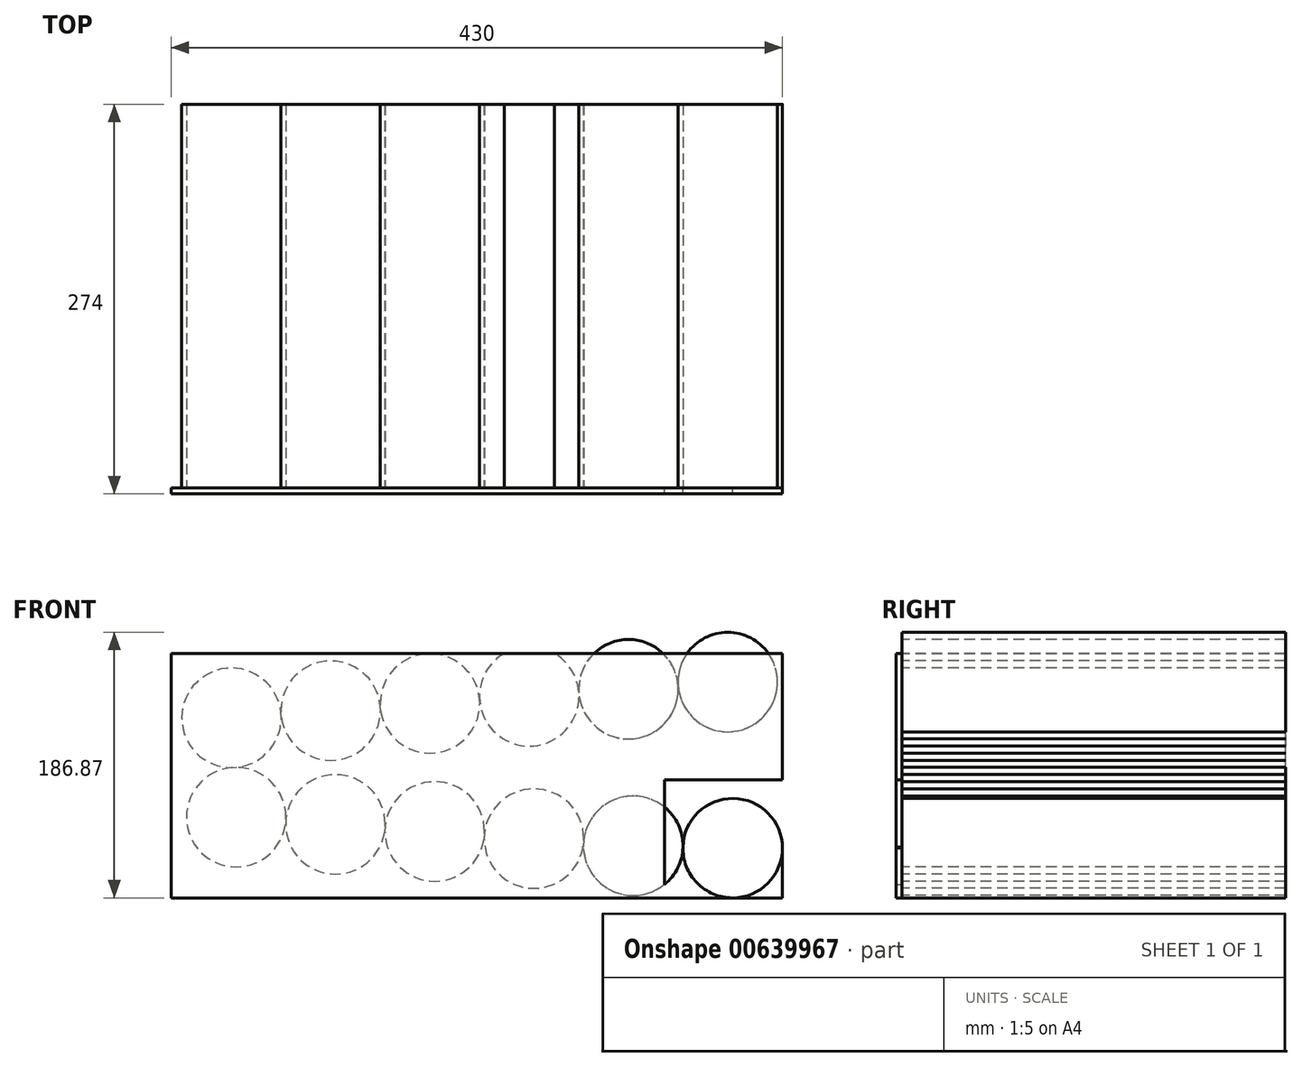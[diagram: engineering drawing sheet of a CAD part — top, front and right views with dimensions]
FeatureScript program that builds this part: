
annotation { "Feature Type Name" : "Feature", "Feature Type Description" : "" }
export const myFeature = defineFeature(function(context is Context, id is Id, definition is map)
    precondition{}
    {
        {
            var Q0;
            Q0=qCreatedBy(makeId("Front.planeOp"),FACE);
            var sketch = newSketch(context, id + "F0", { "sketchPlane" : qUnion([Q0])});
            skLineSegment(sketch, "E0.bottom", {"start": v(-430, 172) * mm, "end": v(0, 172) * mm});
            skLineSegment(sketch, "E0.top", {"start": v(-430, 0) * mm, "end": v(0, 0) * mm});
            skLineSegment(sketch, "E0.left", {"start": v(-430, 172) * mm, "end": v(-430, 0) * mm});
            skLineSegment(sketch, "E0.right", {"start": v(0, 172) * mm, "end": v(0, 0) * mm});
            skCircle(sketch, "E1", {"center": v(-35, 35) * mm, "radius": 35 * mm});
            skCircle(sketch, "E2", {"center": v(-244.62, 46.73) * mm, "radius": 35 * mm});
            skCircle(sketch, "E3", {"center": v(-104.98, 36.67) * mm, "radius": 35 * mm});
            skCircle(sketch, "E4", {"center": v(-174.8, 41.7) * mm, "radius": 35 * mm});
            skLineSegment(sketch, "E5", {"start": v(-430, 25) * mm, "end": v(-83, 0) * mm});
            skCircle(sketch, "E6", {"center": v(-314.44, 51.76) * mm, "radius": 35 * mm});
            skCircle(sketch, "E7", {"center": v(-384.26, 56.8) * mm, "radius": 35 * mm});
            skLineSegment(sketch, "E8", {"start": v(-347, 94.55) * mm, "end": v(0, 119.55) * mm});
            skLineSegment(sketch, "E9", {"start": v(0, 119.55) * mm, "end": v(-430, 119.55) * mm, "construction": true});
            skLineSegment(sketch, "E10", {"start": v(-453.18, 96.16) * mm, "end": v(39.92, 65.4) * mm, "construction": true});
            skLineSegment(sketch, "E11", {"start": v(-465.14, 101.92) * mm, "end": v(33.1, 70.83) * mm, "construction": true});
            skCircle(sketch, "E12", {"center": v(-387.54, 126.72) * mm, "radius": 35 * mm});
            skCircle(sketch, "E13", {"center": v(-317.72, 131.75) * mm, "radius": 35 * mm});
            skCircle(sketch, "E14", {"center": v(-247.9, 136.78) * mm, "radius": 35 * mm});
            skCircle(sketch, "E15", {"center": v(-178.08, 141.8) * mm, "radius": 35 * mm});
            skCircle(sketch, "E16", {"center": v(-108.26, 146.84) * mm, "radius": 35 * mm});
            skCircle(sketch, "E17", {"center": v(-38.44, 151.87) * mm, "radius": 35 * mm});
            skLineSegment(sketch, "E18.bottom", {"start": v(-83, 0) * mm, "end": v(0, 0) * mm});
            skLineSegment(sketch, "E18.top", {"start": v(-83, 83) * mm, "end": v(0, 83) * mm});
            skLineSegment(sketch, "E18.left", {"start": v(-83, 0) * mm, "end": v(-83, 83) * mm});
            skLineSegment(sketch, "E18.right", {"start": v(0, 0) * mm, "end": v(0, 83) * mm});
            skSolve(sketch);
        }
        {
            var Q0;
            {var subQ3=sQuery(id+"F0.wireOp",EDGE,"E0.left");var subQ4=sQuery(id+"F0.wireOp",EDGE,"E0.top");var subQ5=makeQuery(id+"F0.imprint","INTERSECT",VERTEX,{"derivedFrom":[subQ4,subQ3]});Q0=makeQuery(id+"F0.imprint","IMPRINT",FACE,{"disambiguationData":[TD([[makeQuery(id+"F0.imprint","IMPRINT",EDGE,{"disambiguationData":[TD([[subQ5,-1.0]])],"derivedFrom":subQ4}),1.0]])]});}
            var Q1;
            {var subQ0=sQuery(id+"F0.wireOp",EDGE,"E7");var subQ1=sQuery(id+"F0.wireOp",EDGE,"E5");var subQ2=makeQuery(id+"F0.imprint","INTERSECT",VERTEX,{"derivedFrom":[subQ1,subQ0]});Q1=makeQuery(id+"F0.imprint","IMPRINT",FACE,{"disambiguationData":[TD([[makeQuery(id+"F0.imprint","IMPRINT",EDGE,{"disambiguationData":[TD([[subQ2,-1.0]])],"derivedFrom":subQ1}),1.0]])]});}
            var Q2;
            {var subQ0=sQuery(id+"F0.wireOp",EDGE,"E7");var subQ1=makeQuery(id+"F0.imprint","INTERSECT",VERTEX,{"derivedFrom":[sQuery(id+"F0.wireOp",EDGE,"E5"),subQ0]});Q2=makeQuery(id+"F0.imprint","IMPRINT",FACE,{"disambiguationData":[TD([[makeQuery(id+"F0.imprint","IMPRINT",EDGE,{"disambiguationData":[TD([[subQ1,1.0]])],"derivedFrom":subQ0}),1.0]])]});}
            var Q3;
            {var subQ5=sQuery(id+"F0.wireOp",EDGE,"E0.left");var subQ12=sQuery(id+"F0.wireOp",EDGE,"E0.bottom");var subQ13=makeQuery(id+"F0.imprint","INTERSECT",VERTEX,{"derivedFrom":[subQ12,subQ5]});Q3=makeQuery(id+"F0.imprint","IMPRINT",FACE,{"disambiguationData":[TD([[makeQuery(id+"F0.imprint","IMPRINT",EDGE,{"disambiguationData":[TD([[subQ13,-1.0]])],"derivedFrom":subQ12}),-1.0]])]});}
            var Q4;
            {var subQ0=sQuery(id+"F0.wireOp",EDGE,"E6");var subQ1=makeQuery(id+"F0.imprint","INTERSECT",VERTEX,{"derivedFrom":[sQuery(id+"F0.wireOp",EDGE,"E5"),subQ0]});Q4=makeQuery(id+"F0.imprint","IMPRINT",FACE,{"disambiguationData":[TD([[makeQuery(id+"F0.imprint","IMPRINT",EDGE,{"disambiguationData":[TD([[subQ1,1.0]])],"derivedFrom":subQ0}),1.0]])]});}
            var Q5;
            {var subQ0=sQuery(id+"F0.wireOp",EDGE,"E5");var subQ1=sQuery(id+"F0.wireOp",EDGE,"E2");var subQ2=makeQuery(id+"F0.imprint","INTERSECT",VERTEX,{"derivedFrom":[subQ1,subQ0]});Q5=makeQuery(id+"F0.imprint","IMPRINT",FACE,{"disambiguationData":[TD([[makeQuery(id+"F0.imprint","IMPRINT",EDGE,{"disambiguationData":[TD([[subQ2,1.0]])],"derivedFrom":subQ1}),-1.0]])]});}
            var Q6;
            {var subQ0=sQuery(id+"F0.wireOp",EDGE,"E5");var subQ1=sQuery(id+"F0.wireOp",EDGE,"E2");var subQ2=makeQuery(id+"F0.imprint","INTERSECT",VERTEX,{"derivedFrom":[subQ1,subQ0]});Q6=makeQuery(id+"F0.imprint","IMPRINT",FACE,{"disambiguationData":[TD([[makeQuery(id+"F0.imprint","IMPRINT",EDGE,{"disambiguationData":[TD([[subQ2,-1.0]])],"derivedFrom":subQ1}),-1.0]])]});}
            var Q7;
            {var subQ0=sQuery(id+"F0.wireOp",EDGE,"E5");var subQ1=sQuery(id+"F0.wireOp",EDGE,"E3");var subQ2=makeQuery(id+"F0.imprint","INTERSECT",VERTEX,{"derivedFrom":[subQ1,subQ0]});Q7=makeQuery(id+"F0.imprint","IMPRINT",FACE,{"disambiguationData":[TD([[makeQuery(id+"F0.imprint","IMPRINT",EDGE,{"disambiguationData":[TD([[subQ2,1.0]])],"derivedFrom":subQ1}),-1.0]])]});}
            var Q8;
            {var subQ0=sQuery(id+"F0.wireOp",EDGE,"E5");var subQ1=sQuery(id+"F0.wireOp",EDGE,"E0.top");var subQ2=makeQuery(id+"F0.imprint","INTERSECT",VERTEX,{"derivedFrom":[subQ1,subQ0]});Q8=makeQuery(id+"F0.imprint","IMPRINT",FACE,{"disambiguationData":[TD([[makeQuery(id+"F0.imprint","IMPRINT",EDGE,{"disambiguationData":[TD([[subQ2,-1.0]])],"derivedFrom":subQ1}),1.0]])]});}
            var Q9;
            {var subQ0=sQuery(id+"F0.wireOp",EDGE,"E3");var subQ1=makeQuery(id+"F0.imprint","INTERSECT",VERTEX,{"derivedFrom":[subQ0,sQuery(id+"F0.wireOp",EDGE,"E5")]});Q9=makeQuery(id+"F0.imprint","IMPRINT",FACE,{"disambiguationData":[TD([[makeQuery(id+"F0.imprint","IMPRINT",EDGE,{"disambiguationData":[TD([[subQ1,1.0]])],"derivedFrom":subQ0}),1.0]])]});}
            var Q10;
            {var subQ0=sQuery(id+"F0.wireOp",EDGE,"E4");var subQ1=makeQuery(id+"F0.imprint","INTERSECT",VERTEX,{"derivedFrom":[sQuery(id+"F0.wireOp",EDGE,"E2"),subQ0]});Q10=makeQuery(id+"F0.imprint","IMPRINT",FACE,{"disambiguationData":[TD([[makeQuery(id+"F0.imprint","IMPRINT",EDGE,{"disambiguationData":[TD([[subQ1,-1.0]])],"derivedFrom":subQ0}),1.0]])]});}
            var Q11;
            {var subQ0=sQuery(id+"F0.wireOp",EDGE,"E2");var subQ1=makeQuery(id+"F0.imprint","INTERSECT",VERTEX,{"derivedFrom":[subQ0,sQuery(id+"F0.wireOp",EDGE,"E5")]});Q11=makeQuery(id+"F0.imprint","IMPRINT",FACE,{"disambiguationData":[TD([[makeQuery(id+"F0.imprint","IMPRINT",EDGE,{"disambiguationData":[TD([[subQ1,1.0]])],"derivedFrom":subQ0}),1.0]])]});}
            var Q12;
            {var subQ0=sQuery(id+"F0.wireOp",EDGE,"E8");var subQ12=sQuery(id+"F0.wireOp",EDGE,"E0.right");var subQ18=makeQuery(id+"F0.imprint","INTERSECT",VERTEX,{"derivedFrom":[subQ12,subQ0]});Q12=makeQuery(id+"F0.imprint","IMPRINT",FACE,{"disambiguationData":[TD([[makeQuery(id+"F0.imprint","IMPRINT",EDGE,{"disambiguationData":[TD([[subQ18,-1.0]])],"derivedFrom":subQ12}),-1.0]])]});}
            var Q13;
            {var subQ0=sQuery(id+"F0.wireOp",EDGE,"E14");var subQ1=sQuery(id+"F0.wireOp",EDGE,"E8");var subQ2=makeQuery(id+"F0.imprint","INTERSECT",VERTEX,{"derivedFrom":[subQ1,subQ0]});Q13=makeQuery(id+"F0.imprint","IMPRINT",FACE,{"disambiguationData":[TD([[makeQuery(id+"F0.imprint","IMPRINT",EDGE,{"disambiguationData":[TD([[subQ2,-1.0]])],"derivedFrom":subQ1}),1.0]])]});}
            var Q14;
            {var subQ0=sQuery(id+"F0.wireOp",EDGE,"E15");var subQ3=sQuery(id+"F0.wireOp",EDGE,"E0.bottom");var subQ4=makeQuery(id+"F0.imprint","INTERSECT",VERTEX,{"disambiguationData":[OD(0.0)],"derivedFrom":[subQ3,subQ0]});Q14=makeQuery(id+"F0.imprint","IMPRINT",FACE,{"disambiguationData":[TD([[makeQuery(id+"F0.imprint","IMPRINT",EDGE,{"disambiguationData":[TD([[subQ4,-1.0]])],"derivedFrom":subQ3}),-1.0]])]});}
            var Q15;
            {var subQ0=sQuery(id+"F0.wireOp",EDGE,"E16");var subQ3=sQuery(id+"F0.wireOp",EDGE,"E0.bottom");var subQ4=makeQuery(id+"F0.imprint","INTERSECT",VERTEX,{"disambiguationData":[OD(0.0)],"derivedFrom":[subQ3,subQ0]});Q15=makeQuery(id+"F0.imprint","IMPRINT",FACE,{"disambiguationData":[TD([[makeQuery(id+"F0.imprint","IMPRINT",EDGE,{"disambiguationData":[TD([[subQ4,-1.0]])],"derivedFrom":subQ3}),-1.0]])]});}
            var Q16;
            {var subQ0=sQuery(id+"F0.wireOp",EDGE,"E17");var subQ1=sQuery(id+"F0.wireOp",EDGE,"E0.bottom");var subQ2=makeQuery(id+"F0.imprint","INTERSECT",VERTEX,{"disambiguationData":[OD(0.0)],"derivedFrom":[subQ1,subQ0]});Q16=makeQuery(id+"F0.imprint","IMPRINT",FACE,{"disambiguationData":[TD([[makeQuery(id+"F0.imprint","IMPRINT",EDGE,{"disambiguationData":[TD([[subQ2,-1.0]])],"derivedFrom":subQ1}),-1.0]])]});}
            var Q17;
            {var subQ0=sQuery(id+"F0.wireOp",EDGE,"E14");var subQ1=makeQuery(id+"F0.imprint","INTERSECT",VERTEX,{"derivedFrom":[sQuery(id+"F0.wireOp",EDGE,"E13"),subQ0]});Q17=makeQuery(id+"F0.imprint","IMPRINT",FACE,{"disambiguationData":[TD([[makeQuery(id+"F0.imprint","IMPRINT",EDGE,{"disambiguationData":[TD([[subQ1,1.0]])],"derivedFrom":subQ0}),1.0]])]});}
            var Q18;
            {var subQ0=sQuery(id+"F0.wireOp",EDGE,"E13");var subQ1=makeQuery(id+"F0.imprint","INTERSECT",VERTEX,{"derivedFrom":[sQuery(id+"F0.wireOp",EDGE,"E12"),subQ0]});Q18=makeQuery(id+"F0.imprint","IMPRINT",FACE,{"disambiguationData":[TD([[makeQuery(id+"F0.imprint","IMPRINT",EDGE,{"disambiguationData":[TD([[subQ1,1.0]])],"derivedFrom":subQ0}),1.0]])]});}
            var Q19;
            {var subQ0=sQuery(id+"F0.wireOp",EDGE,"E12");var subQ1=makeQuery(id+"F0.imprint","INTERSECT",VERTEX,{"derivedFrom":[sQuery(id+"F0.wireOp",EDGE,"E7"),subQ0]});Q19=makeQuery(id+"F0.imprint","IMPRINT",FACE,{"disambiguationData":[TD([[makeQuery(id+"F0.imprint","IMPRINT",EDGE,{"disambiguationData":[TD([[subQ1,1.0]])],"derivedFrom":subQ0}),1.0]])]});}
            var Q20;
            {var subQ0=sQuery(id+"F0.wireOp",EDGE,"E15");var subQ1=sQuery(id+"F0.wireOp",EDGE,"E8");var subQ2=makeQuery(id+"F0.imprint","INTERSECT",VERTEX,{"derivedFrom":[subQ1,subQ0]});Q20=makeQuery(id+"F0.imprint","IMPRINT",FACE,{"disambiguationData":[TD([[makeQuery(id+"F0.imprint","IMPRINT",EDGE,{"disambiguationData":[TD([[subQ2,-1.0]])],"derivedFrom":subQ1}),1.0]])]});}
            var Q21;
            {var subQ0=sQuery(id+"F0.wireOp",EDGE,"E16");var subQ1=sQuery(id+"F0.wireOp",EDGE,"E8");var subQ2=makeQuery(id+"F0.imprint","INTERSECT",VERTEX,{"derivedFrom":[subQ1,subQ0]});Q21=makeQuery(id+"F0.imprint","IMPRINT",FACE,{"disambiguationData":[TD([[makeQuery(id+"F0.imprint","IMPRINT",EDGE,{"disambiguationData":[TD([[subQ2,-1.0]])],"derivedFrom":subQ1}),1.0]])]});}
            var Q22;
            {var subQ0=sQuery(id+"F0.wireOp",EDGE,"E0.right");var subQ1=sQuery(id+"F0.wireOp",EDGE,"E0.bottom");var subQ2=makeQuery(id+"F0.imprint","INTERSECT",VERTEX,{"derivedFrom":[subQ1,subQ0]});Q22=makeQuery(id+"F0.imprint","IMPRINT",FACE,{"disambiguationData":[TD([[makeQuery(id+"F0.imprint","IMPRINT",EDGE,{"disambiguationData":[TD([[subQ2,1.0]])],"derivedFrom":subQ1}),-1.0]])]});}
            var Q23;
            {var subQ0=sQuery(id+"F0.wireOp",EDGE,"E13");var subQ1=sQuery(id+"F0.wireOp",EDGE,"E8");var subQ2=makeQuery(id+"F0.imprint","INTERSECT",VERTEX,{"derivedFrom":[subQ1,subQ0]});Q23=makeQuery(id+"F0.imprint","IMPRINT",FACE,{"disambiguationData":[TD([[makeQuery(id+"F0.imprint","IMPRINT",EDGE,{"disambiguationData":[TD([[subQ2,-1.0]])],"derivedFrom":subQ1}),1.0]])]});}
            var Q24;
            {var subQ0=sQuery(id+"F0.wireOp",EDGE,"E15");var subQ1=sQuery(id+"F0.wireOp",EDGE,"E0.bottom");var subQ2=makeQuery(id+"F0.imprint","INTERSECT",VERTEX,{"disambiguationData":[OD(1.0)],"derivedFrom":[subQ1,subQ0]});Q24=makeQuery(id+"F0.imprint","IMPRINT",FACE,{"disambiguationData":[TD([[makeQuery(id+"F0.imprint","IMPRINT",EDGE,{"disambiguationData":[TD([[subQ2,-1.0]])],"derivedFrom":subQ1}),-1.0]])]});}
            var Q25;
            {var subQ0=sQuery(id+"F0.wireOp",EDGE,"E16");var subQ1=sQuery(id+"F0.wireOp",EDGE,"E0.bottom");var subQ2=makeQuery(id+"F0.imprint","INTERSECT",VERTEX,{"disambiguationData":[OD(1.0)],"derivedFrom":[subQ1,subQ0]});Q25=makeQuery(id+"F0.imprint","IMPRINT",FACE,{"disambiguationData":[TD([[makeQuery(id+"F0.imprint","IMPRINT",EDGE,{"disambiguationData":[TD([[subQ2,-1.0]])],"derivedFrom":subQ1}),-1.0]])]});}
            var Q26;
            {var subQ0=sQuery(id+"F0.wireOp",EDGE,"E0.right");var subQ1=sQuery(id+"F0.wireOp",EDGE,"E0.top");var subQ2=makeQuery(id+"F0.imprint","INTERSECT",VERTEX,{"derivedFrom":[subQ1,subQ0]});Q26=makeQuery(id+"F0.imprint","IMPRINT",FACE,{"disambiguationData":[TD([[makeQuery(id+"F0.imprint","IMPRINT",EDGE,{"disambiguationData":[TD([[subQ2,1.0]])],"derivedFrom":subQ1}),1.0]])]});}
            var Q27;
            {var subQ0=sQuery(id+"F0.wireOp",EDGE,"E5");var subQ1=sQuery(id+"F0.wireOp",EDGE,"E3");var subQ2=makeQuery(id+"F0.imprint","INTERSECT",VERTEX,{"derivedFrom":[subQ1,subQ0]});Q27=makeQuery(id+"F0.imprint","IMPRINT",FACE,{"disambiguationData":[TD([[makeQuery(id+"F0.imprint","IMPRINT",EDGE,{"disambiguationData":[TD([[subQ2,-1.0]])],"derivedFrom":subQ1}),-1.0]])]});}
            extrude(context, id + "F1", {"entities" : qUnion([Q0, Q1, Q2, Q3, Q4, Q5, Q6, Q7, Q8, Q9, Q10, Q11, Q12, Q13, Q14, Q15, Q16, Q17, Q18, Q19, Q20, Q21, Q22, Q23, Q24, Q25, Q26, Q27]), "depth" : 4 * mm, "offsetDistance" : 25 * mm});
        }
        {
            var Q0;
            {var subQ0=sQuery(id+"F0.wireOp",EDGE,"E7");var subQ1=makeQuery(id+"F0.imprint","INTERSECT",VERTEX,{"derivedFrom":[sQuery(id+"F0.wireOp",EDGE,"E5"),subQ0]});Q0=makeQuery(id+"F0.imprint","IMPRINT",FACE,{"disambiguationData":[TD([[makeQuery(id+"F0.imprint","IMPRINT",EDGE,{"disambiguationData":[TD([[subQ1,1.0]])],"derivedFrom":subQ0}),1.0]])]});}
            var Q1;
            {var subQ0=sQuery(id+"F0.wireOp",EDGE,"E6");var subQ1=makeQuery(id+"F0.imprint","INTERSECT",VERTEX,{"derivedFrom":[sQuery(id+"F0.wireOp",EDGE,"E5"),subQ0]});Q1=makeQuery(id+"F0.imprint","IMPRINT",FACE,{"disambiguationData":[TD([[makeQuery(id+"F0.imprint","IMPRINT",EDGE,{"disambiguationData":[TD([[subQ1,1.0]])],"derivedFrom":subQ0}),1.0]])]});}
            var Q2;
            {var subQ0=sQuery(id+"F0.wireOp",EDGE,"E2");var subQ1=makeQuery(id+"F0.imprint","INTERSECT",VERTEX,{"derivedFrom":[subQ0,sQuery(id+"F0.wireOp",EDGE,"E5")]});Q2=makeQuery(id+"F0.imprint","IMPRINT",FACE,{"disambiguationData":[TD([[makeQuery(id+"F0.imprint","IMPRINT",EDGE,{"disambiguationData":[TD([[subQ1,1.0]])],"derivedFrom":subQ0}),1.0]])]});}
            var Q3;
            {var subQ0=sQuery(id+"F0.wireOp",EDGE,"E4");var subQ1=makeQuery(id+"F0.imprint","INTERSECT",VERTEX,{"derivedFrom":[sQuery(id+"F0.wireOp",EDGE,"E2"),subQ0]});Q3=makeQuery(id+"F0.imprint","IMPRINT",FACE,{"disambiguationData":[TD([[makeQuery(id+"F0.imprint","IMPRINT",EDGE,{"disambiguationData":[TD([[subQ1,-1.0]])],"derivedFrom":subQ0}),1.0]])]});}
            var Q4;
            {var subQ0=sQuery(id+"F0.wireOp",EDGE,"E3");var subQ1=makeQuery(id+"F0.imprint","INTERSECT",VERTEX,{"derivedFrom":[subQ0,sQuery(id+"F0.wireOp",EDGE,"E5")]});Q4=makeQuery(id+"F0.imprint","IMPRINT",FACE,{"disambiguationData":[TD([[makeQuery(id+"F0.imprint","IMPRINT",EDGE,{"disambiguationData":[TD([[subQ1,1.0]])],"derivedFrom":subQ0}),1.0]])]});}
            var Q5;
            {var subQ0=sQuery(id+"F0.wireOp",EDGE,"E1");var subQ1=makeQuery(id+"F0.imprint","INTERSECT",VERTEX,{"derivedFrom":[sQuery(id+"F0.wireOp",EDGE,"E0.right"),subQ0]});Q5=makeQuery(id+"F0.imprint","IMPRINT",FACE,{"disambiguationData":[TD([[makeQuery(id+"F0.imprint","IMPRINT",EDGE,{"disambiguationData":[TD([[subQ1,-1.0]])],"derivedFrom":subQ0}),1.0]])]});}
            var Q6;
            {var subQ0=sQuery(id+"F0.wireOp",EDGE,"E17");var subQ1=sQuery(id+"F0.wireOp",EDGE,"E0.bottom");var subQ2=makeQuery(id+"F0.imprint","INTERSECT",VERTEX,{"disambiguationData":[OD(0.0)],"derivedFrom":[subQ1,subQ0]});Q6=makeQuery(id+"F0.imprint","IMPRINT",FACE,{"disambiguationData":[TD([[makeQuery(id+"F0.imprint","IMPRINT",EDGE,{"disambiguationData":[TD([[subQ2,-1.0]])],"derivedFrom":subQ1}),-1.0]])]});}
            var Q7;
            {var subQ0=sQuery(id+"F0.wireOp",EDGE,"E17");var subQ1=sQuery(id+"F0.wireOp",EDGE,"E0.bottom");var subQ2=makeQuery(id+"F0.imprint","INTERSECT",VERTEX,{"disambiguationData":[OD(0.0)],"derivedFrom":[subQ1,subQ0]});Q7=makeQuery(id+"F0.imprint","IMPRINT",FACE,{"disambiguationData":[TD([[makeQuery(id+"F0.imprint","IMPRINT",EDGE,{"disambiguationData":[TD([[subQ2,-1.0]])],"derivedFrom":subQ1}),1.0]])]});}
            var Q8;
            {var subQ0=sQuery(id+"F0.wireOp",EDGE,"E15");var subQ3=sQuery(id+"F0.wireOp",EDGE,"E0.bottom");var subQ4=makeQuery(id+"F0.imprint","INTERSECT",VERTEX,{"disambiguationData":[OD(0.0)],"derivedFrom":[subQ3,subQ0]});Q8=makeQuery(id+"F0.imprint","IMPRINT",FACE,{"disambiguationData":[TD([[makeQuery(id+"F0.imprint","IMPRINT",EDGE,{"disambiguationData":[TD([[subQ4,-1.0]])],"derivedFrom":subQ3}),-1.0]])]});}
            var Q9;
            {var subQ0=sQuery(id+"F0.wireOp",EDGE,"E14");var subQ1=makeQuery(id+"F0.imprint","INTERSECT",VERTEX,{"derivedFrom":[sQuery(id+"F0.wireOp",EDGE,"E13"),subQ0]});Q9=makeQuery(id+"F0.imprint","IMPRINT",FACE,{"disambiguationData":[TD([[makeQuery(id+"F0.imprint","IMPRINT",EDGE,{"disambiguationData":[TD([[subQ1,1.0]])],"derivedFrom":subQ0}),1.0]])]});}
            var Q10;
            {var subQ0=sQuery(id+"F0.wireOp",EDGE,"E13");var subQ1=makeQuery(id+"F0.imprint","INTERSECT",VERTEX,{"derivedFrom":[sQuery(id+"F0.wireOp",EDGE,"E12"),subQ0]});Q10=makeQuery(id+"F0.imprint","IMPRINT",FACE,{"disambiguationData":[TD([[makeQuery(id+"F0.imprint","IMPRINT",EDGE,{"disambiguationData":[TD([[subQ1,1.0]])],"derivedFrom":subQ0}),1.0]])]});}
            var Q11;
            {var subQ0=sQuery(id+"F0.wireOp",EDGE,"E12");var subQ1=makeQuery(id+"F0.imprint","INTERSECT",VERTEX,{"derivedFrom":[sQuery(id+"F0.wireOp",EDGE,"E7"),subQ0]});Q11=makeQuery(id+"F0.imprint","IMPRINT",FACE,{"disambiguationData":[TD([[makeQuery(id+"F0.imprint","IMPRINT",EDGE,{"disambiguationData":[TD([[subQ1,1.0]])],"derivedFrom":subQ0}),1.0]])]});}
            var Q12;
            {var subQ0=sQuery(id+"F0.wireOp",EDGE,"E16");var subQ3=sQuery(id+"F0.wireOp",EDGE,"E0.bottom");var subQ4=makeQuery(id+"F0.imprint","INTERSECT",VERTEX,{"disambiguationData":[OD(0.0)],"derivedFrom":[subQ3,subQ0]});Q12=makeQuery(id+"F0.imprint","IMPRINT",FACE,{"disambiguationData":[TD([[makeQuery(id+"F0.imprint","IMPRINT",EDGE,{"disambiguationData":[TD([[subQ4,-1.0]])],"derivedFrom":subQ3}),-1.0]])]});}
            var Q13;
            {var subQ0=sQuery(id+"F0.wireOp",EDGE,"E16");var subQ1=sQuery(id+"F0.wireOp",EDGE,"E0.bottom");var subQ2=makeQuery(id+"F0.imprint","INTERSECT",VERTEX,{"disambiguationData":[OD(0.0)],"derivedFrom":[subQ1,subQ0]});Q13=makeQuery(id+"F0.imprint","IMPRINT",FACE,{"disambiguationData":[TD([[makeQuery(id+"F0.imprint","IMPRINT",EDGE,{"disambiguationData":[TD([[subQ2,-1.0]])],"derivedFrom":subQ1}),1.0]])]});}
            var Q14;
            {var subQ0=sQuery(id+"F0.wireOp",EDGE,"E3");var subQ1=makeQuery(id+"F0.imprint","INTERSECT",VERTEX,{"derivedFrom":[sQuery(id+"F0.wireOp",EDGE,"E1"),subQ0]});Q14=makeQuery(id+"F0.imprint","IMPRINT",FACE,{"disambiguationData":[TD([[makeQuery(id+"F0.imprint","IMPRINT",EDGE,{"disambiguationData":[TD([[subQ1,1.0]])],"derivedFrom":subQ0}),1.0]])]});}
            extrude(context, id + "F2", {"entities" : qUnion([Q0, Q1, Q2, Q3, Q4, Q5, Q6, Q7, Q8, Q9, Q10, Q11, Q12, Q13, Q14]), "oppositeDirection" : true, "depth" : 270 * mm, "offsetDistance" : 25 * mm});
        }
    });
